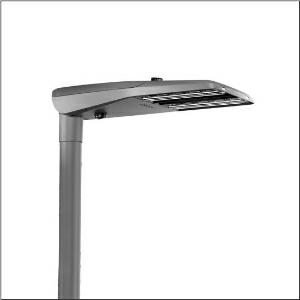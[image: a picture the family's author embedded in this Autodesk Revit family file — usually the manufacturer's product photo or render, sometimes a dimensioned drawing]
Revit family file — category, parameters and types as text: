
# Revit family: streetlight_sl_11_iq_midi___st1_0a_5xc3m51y08me_5fc7
name_source: partatom
category: Lighting Fixtures
units: mm (PartAtom-declared; Revit-internal decimal feet)

## family parameters
Cut with Voids When Loaded = No
Host = Face
Light Source = No
Part Type = Normal
Room Calculation Point = No
Round Connector Dimension = Use Diameter
Shared = No

## types (1)
- --- (1 x LED, 17540 lm, 122.7 W, 3000K)
    Apparent Load = 123 VA
    CIE Flux Codes = 33 66 96 100 100
    Color Rendering = 70
    Color Temperature = 3000K
    Default Elevation = 1800 mm
    Description = Streetlight SL 11 iQ midi, mast luminaire, primary light control with 3 zone facetted reflector, of plastic, silver coated, highly specular, primary optical cover: cover, of PMMA, transparent, light distribution: ST1.0a, light emission: direct distribution, primary light characteristic: asymmetric, installation type: post-top, side-entry, lamps: LED, High Power LED, rated values: 17.540lm | 122,7W | 143lm/W (begin service life); end service life: 17.540lm | 130,2W; at 50% lumin. flux: 8.770lm | 56,1W | 156,3lm/W, colour temperature: 3000K, colour rendering: CRI > 70, light colour: 730, light setting 1 begin service life: 100% | 17.540lm | 122,7W | 143lm/W | 3.000K, light setting 1 end service life: 130,2W, further light settings possible, control: pre-setting: logarithmic dimming characteristic, Street-Remote, Auto-Match, Temp-Guard, Lumen-Switch, Night-Set, Smart-Wire, Light-Fading, Desk-Remote (wireless, voltage-free reading and setting of iQ features in the workshop via application-optimized NFC function/RFID function), optimised constant luminous flux control (CLO 2.0), with cable H07RN-F 5x 1.5mm², mains connection: 230..240V, AC, 50/60Hz, connection cable pre-assembled, cable length: 12,5m, luminaire housing, of diecast aluminium, powder-coated, Siteco® metallic grey (DB 702S), please order mast flange separately, inclination adjustable without tools: 0°, 5°, 10°, 15° (post-top) | 0°, -5°, -10°, -15° (side-entry), sealing non-destructively replaceable, multi-level sealing system, length: 780mm, width: 376mm, height: 118mm, mast flange for spigot size: 42mm (side-entry): 5XC10008XM4, 60/48mm (side-entry/post-top): 5XC10108XM2, 76/60mm (side-entry/post-top): 5XC10108XM1, equipment: Power, Smart Interface below and above, protection rating (complete): IP66, insulation class (complete): insulation class II (safety insulation), certification: CE, ENEC, ENEC+, VDE, UKCA, impact resistance: IK10, permissible operating ambient temperature for outdoor applications: -25..+50°C, standard-compliant lighting for roads and squares, Environmental Product Declaration (EPD) tested and certified by an independent institute, packaging unit: 1 piece

Light Distribution: ST1.0a
    Height = 118 mm
    Lamp = 1 x LED
    Lamp Light Flux = 17540 lm
    Lamp Power = 122.7 W
    Lamp count = 1
    Length = 780 mm
    Luminous efficacy = 143 lm/W
    Manufacturer = Siteco
    ModVariant = No
    Model = 5XC3M51Y08ME
    Number of Poles = 1
    OnlyDefault = Yes
    Power Factor = 1
    Product Name = Streetlight SL 11 iQ midi | ST1.0a
    Product group = mast luminaire | pylon top
    ProductGroupID = 6100
    Protection Class = Protection class II
    Protection Degree = IP 66
    RLX_Detail_Level = 1
    RLX_Emergency_Light_Flux = 0 lm
    RLX_Emergency_Type = 0
    RLX_Emergency_Type_DB = No
    RlxData = <blob elided: 69397 chars, md5=6395d6ea>
    Socket = socket
    Standby Power = 0 W
    System Light Flux = 17540 lm
    System Power = 123 W
    Type Comments = factory setting: luminous flux: 100 % | dim-lin: 254 | 553 mA
    Type Image = l_1004429.jpg
    URL = http://relux.com
    VarID = @adj_109931
    Voltage = 0 V
    Weight = 0.00 kg
    Width = 376 mm

## geometry (parser evidence)
native form markers: Blend x4, Sweep x11
no freeform markers — native parametric forms only
